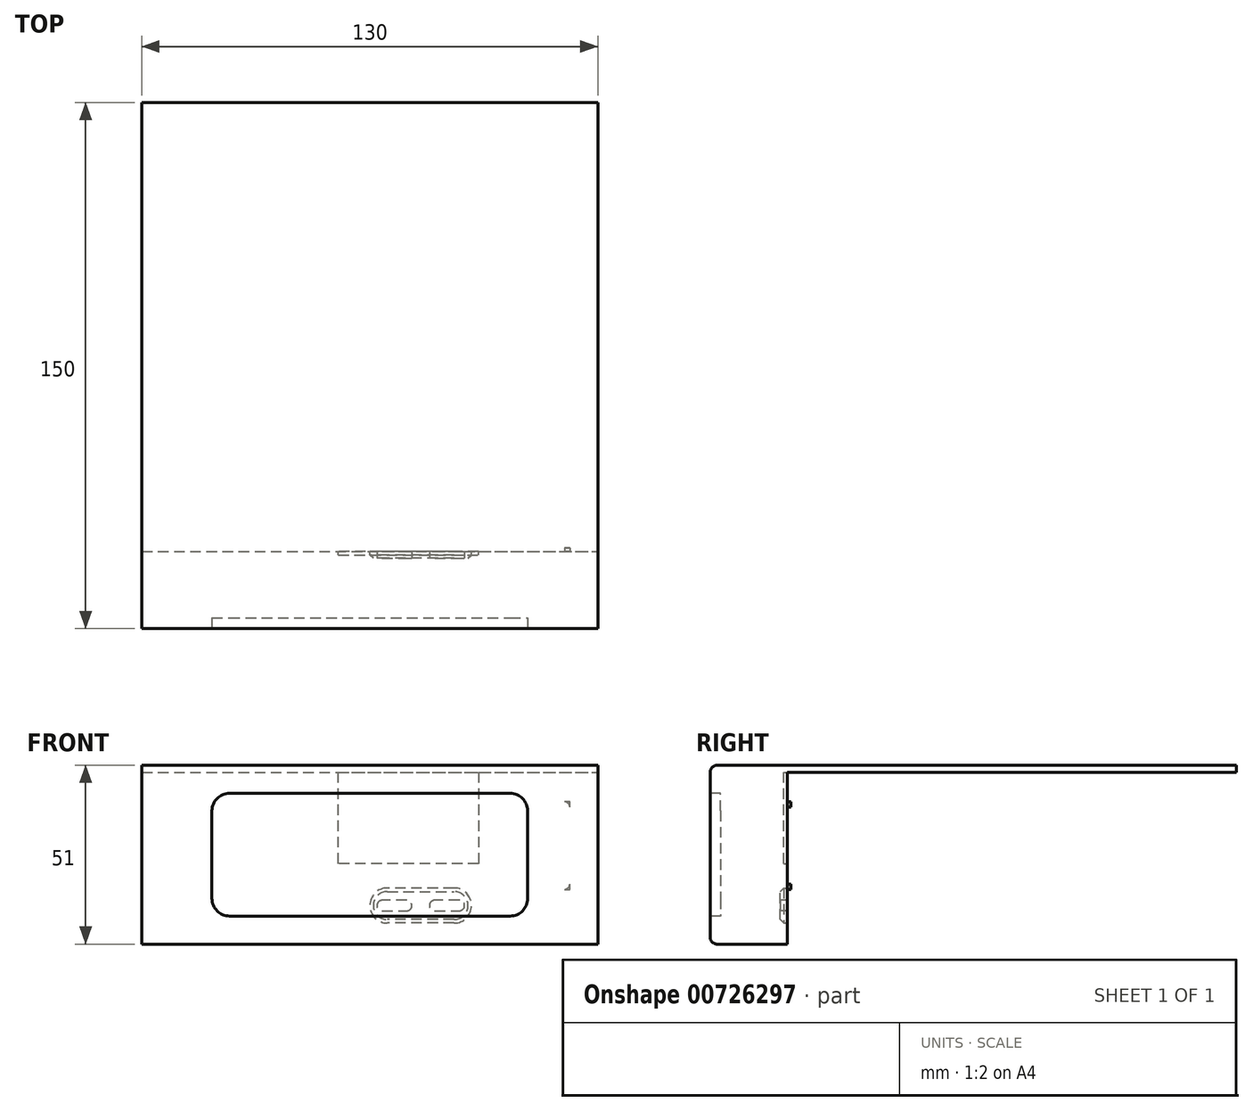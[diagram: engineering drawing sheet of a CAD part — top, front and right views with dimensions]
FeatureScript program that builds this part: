
annotation { "Feature Type Name" : "Feature", "Feature Type Description" : "" }
export const myFeature = defineFeature(function(context is Context, id is Id, definition is map)
    precondition{}
    {
        {
            var Q0;
            Q0=qCreatedBy(makeId("Top.planeOp"),FACE);
            var sketch = newSketch(context, id + "F0", { "sketchPlane" : qUnion([Q0])});
            skLineSegment(sketch, "E0.bottom", {"start": v(65, 75) * mm, "end": v(-65, 75) * mm});
            skLineSegment(sketch, "E0.top", {"start": v(65, -75) * mm, "end": v(-65, -75) * mm});
            skLineSegment(sketch, "E0.left", {"start": v(65, 75) * mm, "end": v(65, -75) * mm});
            skLineSegment(sketch, "E0.right", {"start": v(-65, 75) * mm, "end": v(-65, -75) * mm});
            skPoint(sketch, "E0.middle", {"position": v(0, 0) * mm});
            skSolve(sketch);
        }
        {
            var Q0;
            Q0=makeQuery(id+"F0.imprint","IMPRINT",FACE,{"disambiguationData":[TD([[makeQuery(id+"F0.imprint","IMPRINT",EDGE,{"derivedFrom":sQuery(id+"F0.wireOp",EDGE,"E0.bottom")}),1.0]])]});
            extrude(context, id + "F1", {"entities" : qUnion([Q0]), "depth" : 51 * mm, "offsetDistance" : 25 * mm});
        }
        {
            var Q0;
            Q0=makeQuery(id+"F1.opExtrude","SWEPT_FACE",FACE,{"disambiguationData":[OSD([sQuery(id+"F0.wireOp",EDGE,"E0.left")])]});
            var sketch = newSketch(context, id + "F2", { "sketchPlane" : qUnion([Q0])});
            skLineSegment(sketch, "E1", {"start": v(-75, 0) * mm, "end": v(-53, 0) * mm});
            skLineSegment(sketch, "E2", {"start": v(-53, 0) * mm, "end": v(-53, 49) * mm});
            skLineSegment(sketch, "E3", {"start": v(-53, 49) * mm, "end": v(75, 49) * mm});
            skLineSegment(sketch, "E4", {"start": v(75, 49) * mm, "end": v(75, 51) * mm});
            skSolve(sketch);
        }
        {
            var Q0;
            {var subQ0=sQuery(id+"F2.wireOp",EDGE,"E2");Q0=makeQuery(id+"F2.imprint","IMPRINT",FACE,{"disambiguationData":[TD([[makeQuery(id+"F2.imprint","IMPRINT",EDGE,{"derivedFrom":subQ0}),-1.0]])]});}
            extrude(context, id + "F3", {"entities" : qUnion([Q0]), "operationType" : NewBodyOperationType.REMOVE, "endBound" : BoundingType.THROUGH_ALL, "oppositeDirection" : true, "depth" : 25 * mm, "offsetDistance" : 25 * mm});
        }
        {
            var Q0;
            Q0=makeQuery(id+"F1.opExtrude","SWEPT_FACE",FACE,{"disambiguationData":[OSD([sQuery(id+"F0.wireOp",EDGE,"E0.top")])]});
            var sketch = newSketch(context, id + "F4", { "sketchPlane" : qUnion([Q0])});
            skLineSegment(sketch, "E5", {"start": v(-65, 51) * mm, "end": v(-65, 43) * mm});
            skLineSegment(sketch, "E6", {"start": v(-65, 43) * mm, "end": v(-45, 43) * mm});
            skLineSegment(sketch, "E7", {"start": v(-45, 43) * mm, "end": v(45, 43) * mm});
            skLineSegment(sketch, "E8", {"start": v(-45, 43) * mm, "end": v(-45, 8) * mm});
            skLineSegment(sketch, "E9", {"start": v(-45, 8) * mm, "end": v(45, 8) * mm});
            skLineSegment(sketch, "E10", {"start": v(45, 8) * mm, "end": v(45, 43) * mm});
            skSolve(sketch);
        }
        {
            var Q0;
            Q0=makeQuery(id+"F4.imprint","IMPRINT",FACE,{"disambiguationData":[TD([[makeQuery(id+"F4.imprint","IMPRINT",EDGE,{"derivedFrom":sQuery(id+"F4.wireOp",EDGE,"E7")}),-1.0]])]});
            extrude(context, id + "F5", {"entities" : qUnion([Q0]), "operationType" : NewBodyOperationType.REMOVE, "oppositeDirection" : true, "depth" : 3 * mm, "offsetDistance" : 25 * mm});
        }
        {
            var Q0;
            Q0=makeQuery(id+"F5.boolean.opBoolean","COPY",EDGE,{"derivedFrom":makeQuery(id+"F5.opExtrude","SWEPT_EDGE",EDGE,{"disambiguationData":[OSD([sQuery(id+"F4.wireOp",EDGE,"E7"),sQuery(id+"F4.wireOp",EDGE,"E8")])]})});
            fillet(context, id + "F6", {"entities" : qUnion([Q0]), "radius" : 5 * mm, "tangentPropagation" : true, "allowEdgeOverflow" : false});
        }
        {
            var Q0;
            Q0=makeQuery(id+"F5.boolean.opBoolean","COPY",EDGE,{"derivedFrom":makeQuery(id+"F5.opExtrude","SWEPT_EDGE",EDGE,{"disambiguationData":[OSD([sQuery(id+"F4.wireOp",EDGE,"E7"),sQuery(id+"F4.wireOp",EDGE,"E10")])]})});
            var Q1;
            Q1=makeQuery(id+"F5.boolean.opBoolean","COPY",EDGE,{"derivedFrom":makeQuery(id+"F5.opExtrude","SWEPT_EDGE",EDGE,{"disambiguationData":[OSD([sQuery(id+"F4.wireOp",EDGE,"E9"),sQuery(id+"F4.wireOp",EDGE,"E10")])]})});
            var Q2;
            Q2=makeQuery(id+"F5.boolean.opBoolean","COPY",EDGE,{"derivedFrom":makeQuery(id+"F5.opExtrude","SWEPT_EDGE",EDGE,{"disambiguationData":[OSD([sQuery(id+"F4.wireOp",EDGE,"E8"),sQuery(id+"F4.wireOp",EDGE,"E9")])]})});
            fillet(context, id + "F7", {"entities" : qUnion([Q0, Q1, Q2]), "radius" : 5 * mm, "tangentPropagation" : true, "allowEdgeOverflow" : false});
        }
        {
            var Q0;
            Q0=makeQuery(id+"F1.opExtrude","CAP_EDGE",EDGE,{"disambiguationData":[OSD([sQuery(id+"F0.wireOp",EDGE,"E0.top")])],"isStart":true});
            fillet(context, id + "F8", {"entities" : qUnion([Q0]), "radius" : 2 * mm, "tangentPropagation" : true, "allowEdgeOverflow" : false});
        }
        {
            var Q0;
            Q0=makeQuery(id+"F1.opExtrude","CAP_EDGE",EDGE,{"disambiguationData":[OSD([sQuery(id+"F0.wireOp",EDGE,"E0.top")])],"isStart":false});
            fillet(context, id + "F9", {"entities" : qUnion([Q0]), "radius" : 2 * mm, "tangentPropagation" : true, "allowEdgeOverflow" : false});
        }
        {
            var Q0;
            Q0=makeQuery(id+"F3.boolean.opBoolean","COPY",FACE,{"derivedFrom":makeQuery(id+"F3.opExtrude","SWEPT_FACE",FACE,{"disambiguationData":[OSD([sQuery(id+"F2.wireOp",EDGE,"E2")])]})});
            var sketch = newSketch(context, id + "F10", { "sketchPlane" : qUnion([Q0])});
            skLineSegment(sketch, "E11", {"start": v(-65, 0) * mm, "end": v(-57, 0) * mm});
            skLineSegment(sketch, "E12", {"start": v(-57, 0) * mm, "end": v(-57, 15.6) * mm});
            skLineSegment(sketch, "E13", {"start": v(-57, 15.6) * mm, "end": v(-57, 40.6) * mm});
            skLineSegment(sketch, "E14", {"start": v(-57, 40.6) * mm, "end": v(-54, 40.6) * mm});
            skLineSegment(sketch, "E15", {"start": v(-54, 40.6) * mm, "end": v(-54, 15.6) * mm});
            skLineSegment(sketch, "E16", {"start": v(-54, 15.6) * mm, "end": v(-57, 15.6) * mm});
            skLineSegment(sketch, "E17", {"start": v(-57, 40.6) * mm, "end": v(-57, 39.1) * mm});
            skArc(sketch, "E18", {"start": v(-54, 39.1) * mm, "mid": v(-55.5, 40.6) * mm, "end": v(-57, 39.1) * mm});
            skLineSegment(sketch, "E19", {"start": v(-57, 15.6) * mm, "end": v(-57, 17.1) * mm});
            skArc(sketch, "E20", {"start": v(-57, 17.1) * mm, "mid": v(-55.5, 15.6) * mm, "end": v(-54, 17.1) * mm});
            skSolve(sketch);
        }
        {
            var Q0;
            {var subQ6=sQuery(id+"F10.wireOp",EDGE,"E13");Q0=makeQuery(id+"F10.imprint","IMPRINT",FACE,{"disambiguationData":[TD([[makeQuery(id+"F10.imprint","IMPRINT",EDGE,{"derivedFrom":subQ6}),-1.0]])]});}
            extrude(context, id + "F11", {"entities" : qUnion([Q0]), "operationType" : NewBodyOperationType.ADD, "depth" : 1 * mm, "offsetDistance" : 25 * mm});
        }
        {
            var Q0;
            Q0=makeQuery(id+"F3.boolean.opBoolean","COPY",FACE,{"derivedFrom":makeQuery(id+"F3.opExtrude","SWEPT_FACE",FACE,{"disambiguationData":[OSD([sQuery(id+"F2.wireOp",EDGE,"E2")])]})});
            var sketch = newSketch(context, id + "F12", { "sketchPlane" : qUnion([Q0])});
            skLineSegment(sketch, "E21", {"start": v(-65, 49) * mm, "end": v(-31, 49) * mm});
            skLineSegment(sketch, "E22", {"start": v(-31, 49) * mm, "end": v(-31, 23) * mm});
            skLineSegment(sketch, "E23", {"start": v(-31, 23) * mm, "end": v(9, 23) * mm});
            skLineSegment(sketch, "E24", {"start": v(9, 23) * mm, "end": v(9, 49) * mm});
            skLineSegment(sketch, "E25", {"start": v(-31, 49) * mm, "end": v(-31, 48) * mm});
            skLineSegment(sketch, "E26", {"start": v(-31, 48) * mm, "end": v(9, 48) * mm});
            skSolve(sketch);
        }
        {
            var Q0;
            Q0=makeQuery(id+"F12.imprint","IMPRINT",FACE,{"disambiguationData":[TD([[makeQuery(id+"F12.imprint","IMPRINT",EDGE,{"derivedFrom":sQuery(id+"F12.wireOp",EDGE,"E22")}),1.0]])]});
            extrude(context, id + "F13", {"entities" : qUnion([Q0]), "operationType" : NewBodyOperationType.REMOVE, "oppositeDirection" : true, "depth" : 1 * mm, "offsetDistance" : 25 * mm});
        }
        {
            var Q0;
            Q0=makeQuery(id+"F3.boolean.opBoolean","COPY",FACE,{"derivedFrom":makeQuery(id+"F3.opExtrude","SWEPT_FACE",FACE,{"disambiguationData":[OSD([sQuery(id+"F2.wireOp",EDGE,"E2")])]})});
            var sketch = newSketch(context, id + "F14", { "sketchPlane" : qUnion([Q0])});
            skLineSegment(sketch, "E27", {"start": v(-65, 0) * mm, "end": v(-29, 0) * mm});
            skLineSegment(sketch, "E28", {"start": v(-29, 0) * mm, "end": v(-29, 6) * mm});
            skLineSegment(sketch, "E29", {"start": v(-29, 6) * mm, "end": v(-29, 16) * mm});
            skLineSegment(sketch, "E30", {"start": v(-29, 16) * mm, "end": v(0, 16) * mm});
            skLineSegment(sketch, "E31", {"start": v(-29, 6) * mm, "end": v(0, 6) * mm});
            skLineSegment(sketch, "E32", {"start": v(0, 6) * mm, "end": v(0, 16) * mm});
            skLineSegment(sketch, "E33", {"start": v(-29, 6) * mm, "end": v(-24, 6) * mm});
            skLineSegment(sketch, "E34", {"start": v(-24, 6) * mm, "end": v(-24, 16) * mm});
            skArc(sketch, "E35", {"start": v(-24, 16) * mm, "mid": v(-29, 11) * mm, "end": v(-24, 6) * mm});
            skLineSegment(sketch, "E36", {"start": v(0, 16) * mm, "end": v(-5, 16) * mm});
            skArc(sketch, "E37", {"start": v(-5, 6) * mm, "mid": v(0, 11) * mm, "end": v(-5, 16) * mm});
            skSolve(sketch);
        }
        {
            var Q0;
            {var subQ0=sQuery(id+"F14.wireOp",EDGE,"E34");Q0=makeQuery(id+"F14.imprint","IMPRINT",FACE,{"disambiguationData":[TD([[makeQuery(id+"F14.imprint","IMPRINT",EDGE,{"derivedFrom":subQ0}),-1.0]])]});}
            var Q1;
            {var subQ0=sQuery(id+"F14.wireOp",EDGE,"E34");Q1=makeQuery(id+"F14.imprint","IMPRINT",FACE,{"disambiguationData":[TD([[makeQuery(id+"F14.imprint","IMPRINT",EDGE,{"derivedFrom":subQ0}),1.0]])]});}
            extrude(context, id + "F15", {"entities" : qUnion([Q0, Q1]), "operationType" : NewBodyOperationType.REMOVE, "oppositeDirection" : true, "depth" : 2 * mm, "offsetDistance" : 25 * mm});
        }
        {
            var Q0;
            Q0=makeQuery(id+"F15.boolean.opBoolean","COPY",EDGE,{"derivedFrom":makeQuery(id+"F15.opExtrude","CAP_EDGE",EDGE,{"disambiguationData":[OSD([sQuery(id+"F14.wireOp",EDGE,"E35")])],"isStart":false})});
            var Q1;
            Q1=makeQuery(id+"F15.boolean.opBoolean","COPY",EDGE,{"derivedFrom":makeQuery(id+"F15.opExtrude","CAP_EDGE",EDGE,{"disambiguationData":[OSD([sQuery(id+"F14.wireOp",EDGE,"E30")])],"isStart":false})});
            var Q2;
            Q2=makeQuery(id+"F15.boolean.opBoolean","COPY",EDGE,{"derivedFrom":makeQuery(id+"F15.opExtrude","CAP_EDGE",EDGE,{"disambiguationData":[OSD([sQuery(id+"F14.wireOp",EDGE,"E37")])],"isStart":false})});
            var Q3;
            Q3=makeQuery(id+"F15.boolean.opBoolean","COPY",EDGE,{"derivedFrom":makeQuery(id+"F15.opExtrude","CAP_EDGE",EDGE,{"disambiguationData":[OSD([sQuery(id+"F14.wireOp",EDGE,"E31")])],"isStart":false})});
            chamfer(context, id + "F16", {"entities" : qUnion([Q0, Q1, Q2, Q3]), "width" : 1 * mm, "tangentPropagation" : true});
        }
        {
            var Q0;
            Q0=makeQuery(id+"F15.boolean.opBoolean","COPY",FACE,{"derivedFrom":makeQuery(id+"F15.opExtrude","CAP_FACE",FACE,{"disambiguationData":[OSD([sQuery(id+"F14.wireOp",EDGE,"E30"),sQuery(id+"F14.wireOp",EDGE,"E31"),sQuery(id+"F14.wireOp",EDGE,"E35"),sQuery(id+"F14.wireOp",EDGE,"E37")])],"isStart":false})});
            var sketch = newSketch(context, id + "F17", { "sketchPlane" : qUnion([Q0])});
            skLineSegment(sketch, "E38", {"start": v(-24, 11) * mm, "end": v(-27, 11) * mm});
            skLineSegment(sketch, "E39", {"start": v(-24, 11) * mm, "end": v(-17, 11) * mm});
            skLineSegment(sketch, "E40", {"start": v(-27, 11) * mm, "end": v(-27, 12.5) * mm});
            skLineSegment(sketch, "E41", {"start": v(-27, 11) * mm, "end": v(-27, 9.5) * mm});
            skLineSegment(sketch, "E42", {"start": v(-27, 12.5) * mm, "end": v(-17, 12.5) * mm});
            skLineSegment(sketch, "E43", {"start": v(-17, 12.5) * mm, "end": v(-17, 9.5) * mm});
            skLineSegment(sketch, "E44", {"start": v(-17, 9.5) * mm, "end": v(-27, 9.5) * mm});
            skLineSegment(sketch, "E45", {"start": v(-27, 12.5) * mm, "end": v(-27, 13.02) * mm});
            skLineSegment(sketch, "E46", {"start": v(-27, 13.02) * mm, "end": v(-25.5, 13.02) * mm});
            skArc(sketch, "E47", {"start": v(-25.5, 12.5) * mm, "mid": v(-27, 11) * mm, "end": v(-25.5, 9.5) * mm});
            skLineSegment(sketch, "E48", {"start": v(-17, 9.5) * mm, "end": v(-17, 8.83) * mm});
            skLineSegment(sketch, "E49", {"start": v(-17, 8.83) * mm, "end": v(-18.5, 8.83) * mm});
            skArc(sketch, "E50", {"start": v(-18.5, 9.5) * mm, "mid": v(-17, 11) * mm, "end": v(-18.5, 12.5) * mm});
            skLineSegment(sketch, "E51", {"start": v(-12, 10.98) * mm, "end": v(-12, 12.48) * mm});
            skLineSegment(sketch, "E52", {"start": v(-12, 10.98) * mm, "end": v(-12, 9.48) * mm});
            skLineSegment(sketch, "E53", {"start": v(-12, 12.48) * mm, "end": v(-2, 12.48) * mm});
            skLineSegment(sketch, "E54", {"start": v(-2, 12.48) * mm, "end": v(-2, 9.48) * mm});
            skLineSegment(sketch, "E55", {"start": v(-2, 9.48) * mm, "end": v(-12, 9.48) * mm});
            skLineSegment(sketch, "E56", {"start": v(-12, 12.48) * mm, "end": v(-12, 13) * mm});
            skLineSegment(sketch, "E57", {"start": v(-12, 13) * mm, "end": v(-10.5, 13) * mm});
            skArc(sketch, "E58", {"start": v(-10.5, 12.48) * mm, "mid": v(-12, 10.98) * mm, "end": v(-10.5, 9.48) * mm});
            skLineSegment(sketch, "E59", {"start": v(-2, 9.48) * mm, "end": v(-2, 8.8) * mm});
            skLineSegment(sketch, "E60", {"start": v(-2, 8.8) * mm, "end": v(-3.5, 8.8) * mm});
            skArc(sketch, "E61", {"start": v(-3.5, 9.48) * mm, "mid": v(-2, 10.98) * mm, "end": v(-3.5, 12.48) * mm});
            skSolve(sketch);
        }
        {
            var Q0;
            {var subQ1=sQuery(id+"F17.wireOp",EDGE,"E38");Q0=makeQuery(id+"F17.imprint","IMPRINT",FACE,{"disambiguationData":[TD([[makeQuery(id+"F17.imprint","IMPRINT",EDGE,{"derivedFrom":subQ1}),-1.0]])]});}
            var Q1;
            {var subQ1=sQuery(id+"F17.wireOp",EDGE,"E38");Q1=makeQuery(id+"F17.imprint","IMPRINT",FACE,{"disambiguationData":[TD([[makeQuery(id+"F17.imprint","IMPRINT",EDGE,{"derivedFrom":subQ1}),1.0]])]});}
            var Q2;
            {var subQ0=sQuery(id+"F17.wireOp",EDGE,"E58");var subQ4=sQuery(id+"F17.wireOp",EDGE,"E53");var subQ5=makeQuery(id+"F17.imprint","INTERSECT",VERTEX,{"derivedFrom":[subQ4,subQ0]});Q2=makeQuery(id+"F17.imprint","IMPRINT",FACE,{"disambiguationData":[TD([[makeQuery(id+"F17.imprint","IMPRINT",EDGE,{"disambiguationData":[TD([[subQ5,-1.0]])],"derivedFrom":subQ4}),-1.0]])]});}
            extrude(context, id + "F18", {"entities" : qUnion([Q0, Q1, Q2]), "operationType" : NewBodyOperationType.ADD, "depth" : 2 * mm, "offsetDistance" : 25 * mm});
        }
    });
